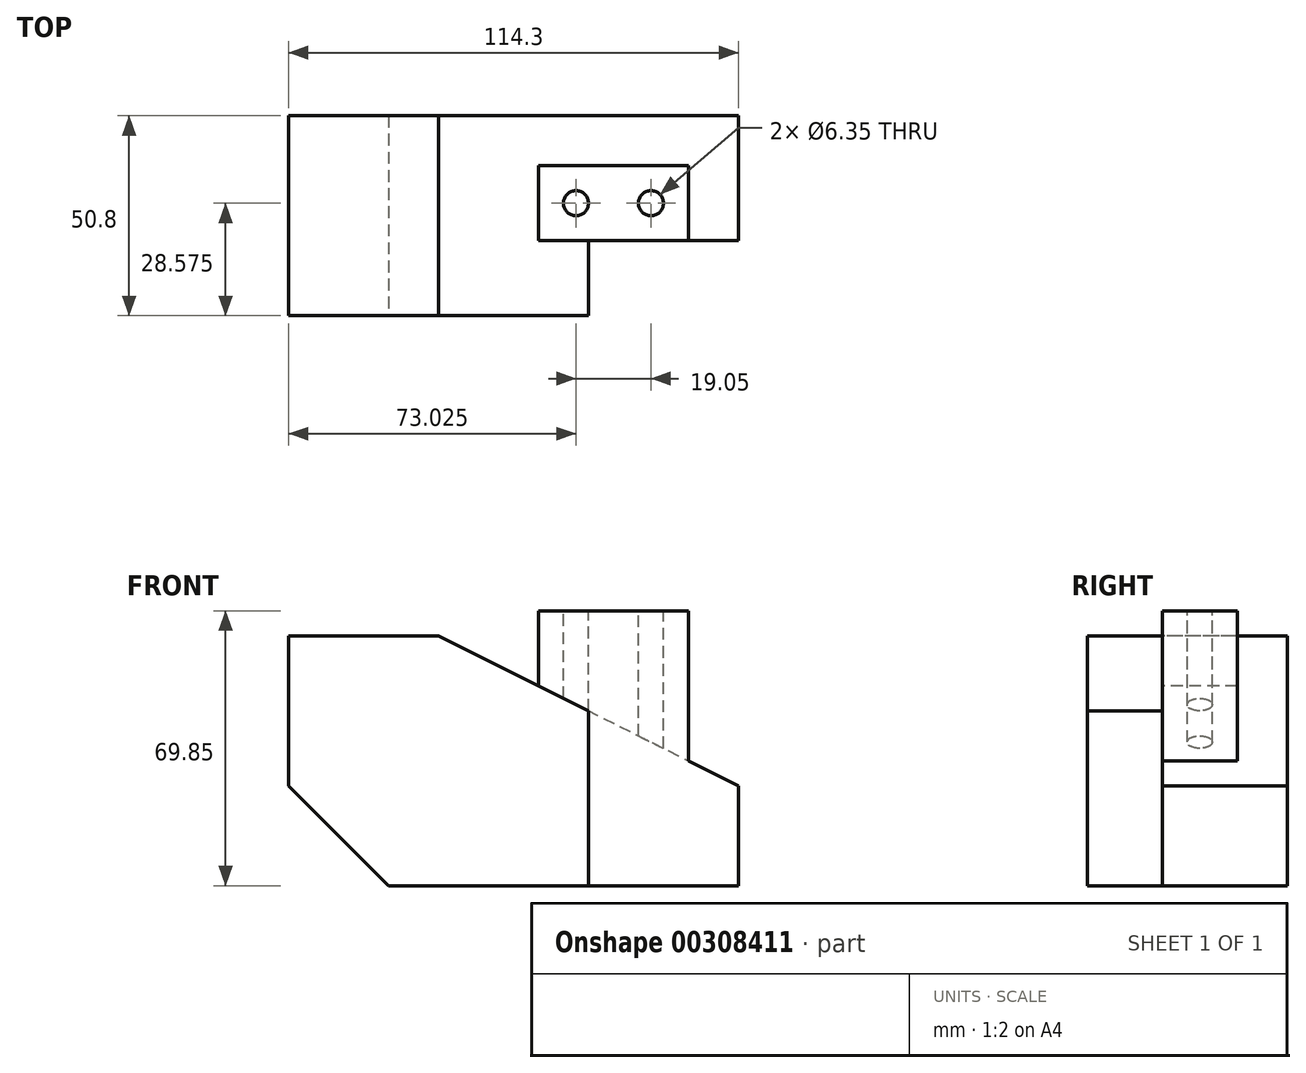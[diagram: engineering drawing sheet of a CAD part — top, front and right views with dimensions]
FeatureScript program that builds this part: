
annotation { "Feature Type Name" : "Feature", "Feature Type Description" : "" }
export const myFeature = defineFeature(function(context is Context, id is Id, definition is map)
    precondition{}
    {
        {
            var Q0;
            Q0=qCreatedBy(makeId("Front.planeOp"),FACE);
            var sketch = newSketch(context, id + "F0", { "sketchPlane" : qUnion([Q0])});
            skLineSegment(sketch, "E0.bottom", {"start": v(0, 0) * mm, "end": v(114.3, 0) * mm});
            skLineSegment(sketch, "E0.top", {"start": v(0, 69.85) * mm, "end": v(114.3, 69.85) * mm});
            skLineSegment(sketch, "E0.left", {"start": v(0, 0) * mm, "end": v(0, 69.85) * mm});
            skLineSegment(sketch, "E0.right", {"start": v(114.3, 0) * mm, "end": v(114.3, 69.85) * mm});
            skSolve(sketch);
        }
        {
            var Q0;
            Q0 = qSketchRegion(id + "F0", true);
            extrude(context, id + "F1", {"entities" : qUnion([Q0]), "oppositeDirection" : true, "depth" : 50.8 * mm});
        }
        {
            var Q0;
            Q0=makeQuery(id+"F1.opExtrude","CAP_FACE",FACE,{"disambiguationData":[OSD([sQuery(id+"F0.wireOp",EDGE,"E0.bottom"),sQuery(id+"F0.wireOp",EDGE,"E0.top"),sQuery(id+"F0.wireOp",EDGE,"E0.left"),sQuery(id+"F0.wireOp",EDGE,"E0.right")])],"isStart":true});
            var sketch = newSketch(context, id + "F2", { "sketchPlane" : qUnion([Q0])});
            skLineSegment(sketch, "E1", {"start": v(0, 25.4) * mm, "end": v(25.4, 0) * mm});
            skLineSegment(sketch, "E2", {"start": v(114.3, 25.4) * mm, "end": v(114.3, 0) * mm});
            skLineSegment(sketch, "E3", {"start": v(101.6, 31.75) * mm, "end": v(114.3, 25.4) * mm});
            skLineSegment(sketch, "E4", {"start": v(0, 63.5) * mm, "end": v(38.1, 63.5) * mm});
            skLineSegment(sketch, "E5", {"start": v(101.6, 31.75) * mm, "end": v(101.6, 69.85) * mm});
            skLineSegment(sketch, "E6", {"start": v(101.6, 69.85) * mm, "end": v(63.5, 69.85) * mm});
            skLineSegment(sketch, "E7", {"start": v(0, 69.85) * mm, "end": v(0, 63.5) * mm});
            skLineSegment(sketch, "E8", {"start": v(38.1, 63.5) * mm, "end": v(63.5, 50.8) * mm});
            skLineSegment(sketch, "E9", {"start": v(76.2, 44.45) * mm, "end": v(76.2, 0) * mm});
            skLineSegment(sketch, "E10", {"start": v(63.5, 69.85) * mm, "end": v(63.5, 50.8) * mm});
            skLineSegment(sketch, "E11", {"start": v(63.5, 50.8) * mm, "end": v(76.2, 44.45) * mm});
            skSolve(sketch);
        }
        {
            var Q0;
            Q0=makeQuery(id+"F2.imprint","IMPRINT",FACE,{"disambiguationData":[TD([[makeQuery(id+"F2.imprint","IMPRINT",EDGE,{"derivedFrom":sQuery(id+"F2.wireOp",EDGE,"E4")}),1.0]])]});
            var Q1;
            {var subQ0=sQuery(id+"F2.wireOp",EDGE,"E1");Q1=makeQuery(id+"F2.imprint","IMPRINT",FACE,{"disambiguationData":[TD([[makeQuery(id+"F2.imprint","IMPRINT",EDGE,{"derivedFrom":subQ0}),-1.0]])]});}
            var Q2;
            {var subQ0=sQuery(id+"F2.wireOp",EDGE,"E5");Q2=makeQuery(id+"F2.imprint","IMPRINT",FACE,{"disambiguationData":[TD([[makeQuery(id+"F2.imprint","IMPRINT",EDGE,{"derivedFrom":subQ0}),-1.0]])]});}
            extrude(context, id + "F3", {"entities" : qUnion([Q0, Q1, Q2]), "operationType" : NewBodyOperationType.REMOVE, "endBound" : BoundingType.THROUGH_ALL, "oppositeDirection" : true, "depth" : 25.4 * mm});
        }
        {
            var Q0;
            {var subQ1=sQuery(id+"F2.wireOp",EDGE,"E5");Q0=makeQuery(id+"F2.imprint","IMPRINT",FACE,{"disambiguationData":[TD([[makeQuery(id+"F2.imprint","IMPRINT",EDGE,{"derivedFrom":subQ1}),1.0]])]});}
            extrude(context, id + "F4", {"entities" : qUnion([Q0]), "operationType" : NewBodyOperationType.REMOVE, "oppositeDirection" : true, "depth" : 19.05 * mm});
        }
        {
            var Q0;
            Q0=makeQuery(id+"F3.boolean.opBoolean","COPY",FACE,{"derivedFrom":makeQuery(id+"F3.opExtrude","SWEPT_FACE",FACE,{"disambiguationData":[OSD([sQuery(id+"F2.wireOp",EDGE,"E5")])]})});
            var sketch = newSketch(context, id + "F5", { "sketchPlane" : qUnion([Q0])});
            skLineSegment(sketch, "E12.bottom", {"start": v(19.05, 69.85) * mm, "end": v(38.1, 69.85) * mm});
            skLineSegment(sketch, "E12.top", {"start": v(19.05, 31.75) * mm, "end": v(38.1, 31.75) * mm});
            skLineSegment(sketch, "E12.left", {"start": v(19.05, 69.85) * mm, "end": v(19.05, 31.75) * mm});
            skLineSegment(sketch, "E12.right", {"start": v(38.1, 69.85) * mm, "end": v(38.1, 31.75) * mm});
            skSolve(sketch);
        }
        {
            var Q0;
            {var subQ0=sQuery(id+"F5.wireOp",EDGE,"E12.right");Q0=makeQuery(id+"F5.imprint","IMPRINT",FACE,{"disambiguationData":[TD([[makeQuery(id+"F5.imprint","IMPRINT",EDGE,{"derivedFrom":subQ0}),1.0]])]});}
            var Q1;
            Q1=makeQuery(id+"F4.boolean.opBoolean","MERGE",FACE,{"derivedFrom":[makeQuery(id+"F3.boolean.opBoolean","COPY",FACE,{"derivedFrom":makeQuery(id+"F3.opExtrude","SWEPT_FACE",FACE,{"disambiguationData":[OSD([sQuery(id+"F2.wireOp",EDGE,"E8")])]})}),makeQuery(id+"F4.opExtrude","SWEPT_FACE",FACE,{"disambiguationData":[OSD([sQuery(id+"F2.wireOp",EDGE,"E11")])]})]});
            extrude(context, id + "F6", {"entities" : qUnion([Q0]), "operationType" : NewBodyOperationType.REMOVE, "endBound" : BoundingType.UP_TO_SURFACE, "oppositeDirection" : true, "endBoundEntityFace" : qUnion([Q1]), "depth" : 25.4 * mm});
        }
        {
            var Q0;
            Q0=makeQuery(id+"F1.opExtrude","SWEPT_FACE",FACE,{"disambiguationData":[OSD([sQuery(id+"F0.wireOp",EDGE,"E0.top")])]});
            var sketch = newSketch(context, id + "F7", { "sketchPlane" : qUnion([Q0])});
            skCircle(sketch, "E13", {"center": v(73.03, 28.57) * mm, "radius": 3.18 * mm});
            skCircle(sketch, "E14", {"center": v(92.07, 28.57) * mm, "radius": 3.18 * mm});
            skSolve(sketch);
        }
        {
            var Q0;
            Q0 = qSketchRegion(id + "F7", true);
            var Q1;
            {var subQ0=sQuery(id+"F2.wireOp",EDGE,"E11");var subQ1=sQuery(id+"F2.wireOp",EDGE,"E8");Q1=makeQuery(id+"F6.boolean.opBoolean","MERGE",FACE,{"derivedFrom":[makeQuery(id+"F4.boolean.opBoolean","MERGE",FACE,{"derivedFrom":[makeQuery(id+"F3.boolean.opBoolean","COPY",FACE,{"derivedFrom":makeQuery(id+"F3.opExtrude","SWEPT_FACE",FACE,{"disambiguationData":[OSD([subQ1])]})}),makeQuery(id+"F4.opExtrude","SWEPT_FACE",FACE,{"disambiguationData":[OSD([subQ0])]})]}),makeQuery(id+"F3.boolean.opBoolean","COPY",FACE,{"derivedFrom":makeQuery(id+"F3.opExtrude","SWEPT_FACE",FACE,{"disambiguationData":[OSD([sQuery(id+"F2.wireOp",EDGE,"E3")])]})}),makeQuery(id+"F6.opExtrude","CAP_FACE",FACE,{"disambiguationData":[OSD([subQ1,subQ0])],"isStart":false})]});}
            extrude(context, id + "F8", {"entities" : qUnion([Q0]), "operationType" : NewBodyOperationType.REMOVE, "endBound" : BoundingType.UP_TO_SURFACE, "oppositeDirection" : true, "endBoundEntityFace" : qUnion([Q1]), "depth" : 25.4 * mm});
        }
    });
